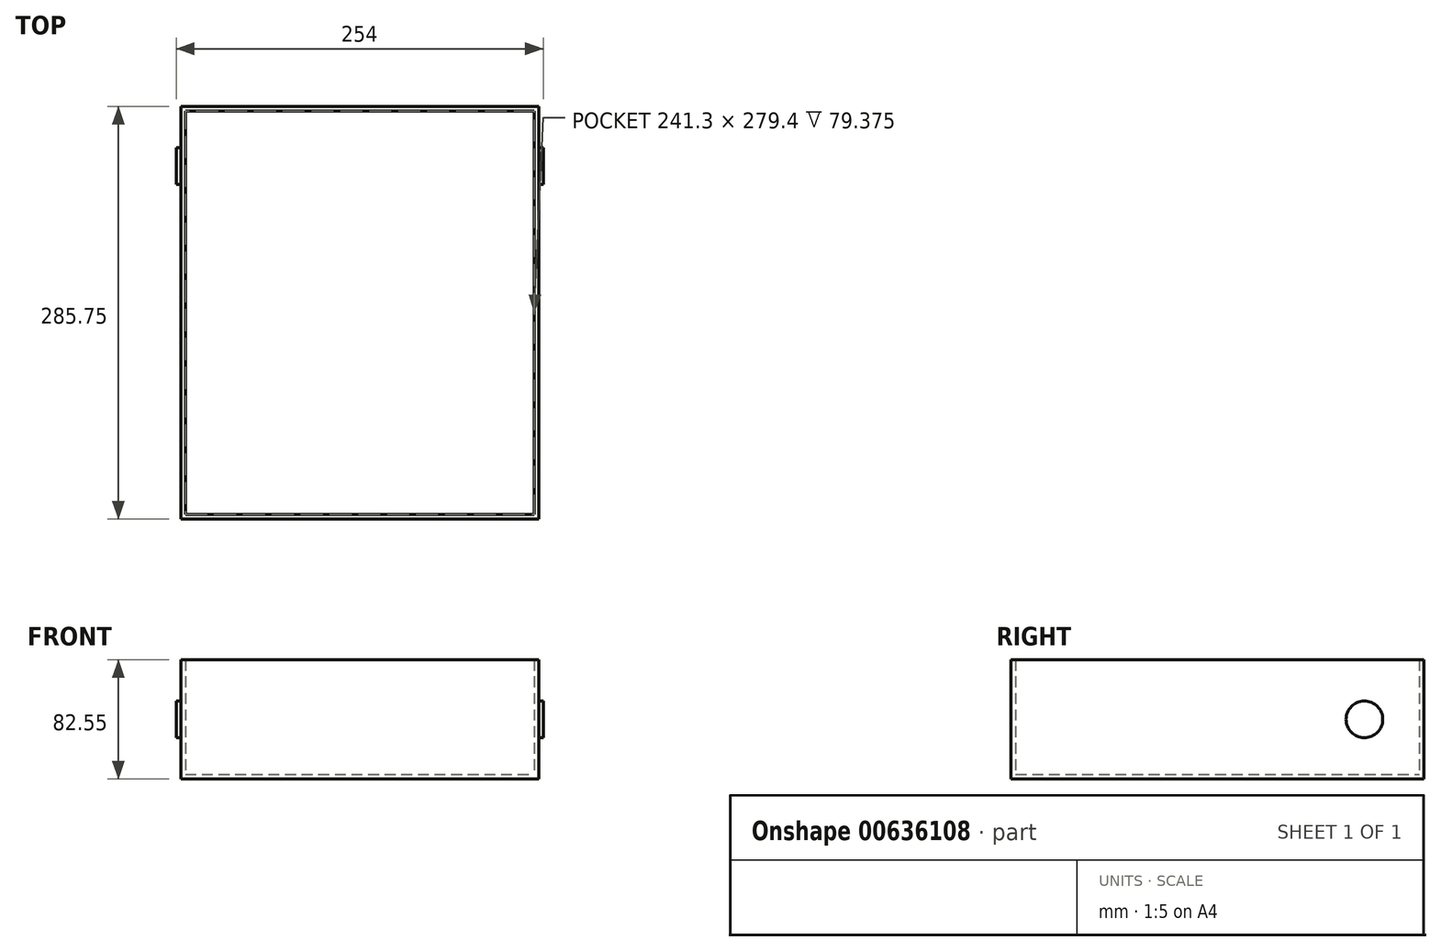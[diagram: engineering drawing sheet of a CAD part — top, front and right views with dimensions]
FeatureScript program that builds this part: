
annotation { "Feature Type Name" : "Feature", "Feature Type Description" : "" }
export const myFeature = defineFeature(function(context is Context, id is Id, definition is map)
    precondition{}
    {
        {
            var Q0;
            Q0=qCreatedBy(makeId("Top.planeOp"),FACE);
            var sketch = newSketch(context, id + "F0", { "sketchPlane" : qUnion([Q0])});
            skLineSegment(sketch, "E0.right", {"start": v(-132.22, 90.63) * mm, "end": v(-132.22, -188.77) * mm});
            skLineSegment(sketch, "E1.top", {"start": v(-132.22, 93.8) * mm, "end": v(112.25, 93.8) * mm});
            skLineSegment(sketch, "E1.left", {"start": v(-132.22, 90.63) * mm, "end": v(-132.22, 93.8) * mm});
            skLineSegment(sketch, "E2.bottom", {"start": v(112.25, 93.8) * mm, "end": v(115.43, 93.8) * mm});
            skLineSegment(sketch, "E2.right", {"start": v(115.43, 93.8) * mm, "end": v(115.43, -188.77) * mm});
            skLineSegment(sketch, "E3.top", {"start": v(-132.22, -191.95) * mm, "end": v(115.43, -191.95) * mm});
            skLineSegment(sketch, "E3.left", {"start": v(-132.22, -188.77) * mm, "end": v(-132.22, -191.95) * mm});
            skLineSegment(sketch, "E3.right", {"start": v(115.43, -188.77) * mm, "end": v(115.43, -191.95) * mm});
            skPoint(sketch, "E4.right.end.orphan", {"position": v(112.25, -188.77) * mm});
            skPoint(sketch, "E4.left.end.orphan", {"position": v(-129.05, -188.77) * mm});
            skPoint(sketch, "E4.bottom.end.orphan", {"position": v(112.25, 90.63) * mm});
            skSolve(sketch);
        }
        {
            var Q0;
            Q0=makeQuery(id+"F0.imprint","IMPRINT",FACE,{"disambiguationData":[TD([[makeQuery(id+"F0.imprint","IMPRINT",EDGE,{"derivedFrom":sQuery(id+"F0.wireOp",EDGE,"E0.right")}),1.0]])]});
            extrude(context, id + "F1", {"entities" : qUnion([Q0]), "depth" : 82.55 * mm, "offsetDistance" : 25.4 * mm});
        }
        {
            var Q0;
            Q0=makeQuery(id+"F1.opExtrude","CAP_FACE",FACE,{"disambiguationData":[OSD([sQuery(id+"F0.wireOp",EDGE,"E0.right"),sQuery(id+"F0.wireOp",EDGE,"E1.top"),sQuery(id+"F0.wireOp",EDGE,"E1.left"),sQuery(id+"F0.wireOp",EDGE,"E2.bottom"),sQuery(id+"F0.wireOp",EDGE,"E2.right"),sQuery(id+"F0.wireOp",EDGE,"E3.top"),sQuery(id+"F0.wireOp",EDGE,"E3.left"),sQuery(id+"F0.wireOp",EDGE,"E3.right")])],"isStart":false});
            shell(context, id + "F2", {"entities" : qUnion([Q0]), "thickness" : 3.17 * mm});
        }
        {
            var Q0;
            Q0=makeQuery(id+"F1.opExtrude","SWEPT_FACE",FACE,{"disambiguationData":[OSD([sQuery(id+"F0.wireOp",EDGE,"E2.right"),sQuery(id+"F0.wireOp",EDGE,"E3.right")])]});
            var sketch = newSketch(context, id + "F3", { "sketchPlane" : qUnion([Q0])});
            skLineSegment(sketch, "E5", {"start": v(93.8, 41.28) * mm, "end": v(65.23, 41.28) * mm});
            skLineSegment(sketch, "E6", {"start": v(52.53, 53.98) * mm, "end": v(52.53, 82.55) * mm});
            skCircle(sketch, "E7", {"center": v(52.53, 41.28) * mm, "radius": 12.7 * mm});
            skSolve(sketch);
        }
        {
            var Q0;
            Q0=makeQuery(id+"F1.opExtrude","SWEPT_FACE",FACE,{"disambiguationData":[OSD([sQuery(id+"F0.wireOp",EDGE,"E0.right"),sQuery(id+"F0.wireOp",EDGE,"E1.left"),sQuery(id+"F0.wireOp",EDGE,"E3.left")])]});
            var sketch = newSketch(context, id + "F4", { "sketchPlane" : qUnion([Q0])});
            skLineSegment(sketch, "E8", {"start": v(-93.8, 41.28) * mm, "end": v(-65.23, 41.28) * mm});
            skLineSegment(sketch, "E9", {"start": v(-52.53, 53.98) * mm, "end": v(-52.53, 82.55) * mm});
            skCircle(sketch, "E10", {"center": v(-52.53, 41.28) * mm, "radius": 12.7 * mm});
            skSolve(sketch);
        }
        {
            var Q0;
            {var subQ0=sQuery(id+"F3.wireOp",EDGE,"E7");var subQ1=makeQuery(id+"F3.imprint","INTERSECT",VERTEX,{"derivedFrom":[sQuery(id+"F3.wireOp",EDGE,"E5"),subQ0]});Q0=makeQuery(id+"F3.imprint","IMPRINT",FACE,{"disambiguationData":[TD([[makeQuery(id+"F3.imprint","IMPRINT",EDGE,{"disambiguationData":[TD([[subQ1,-1.0]])],"derivedFrom":subQ0}),1.0]])]});}
            extrude(context, id + "F5", {"entities" : qUnion([Q0]), "operationType" : NewBodyOperationType.ADD, "depth" : 3.17 * mm, "offsetDistance" : 25.4 * mm});
        }
        {
            var Q0;
            {var subQ0=sQuery(id+"F4.wireOp",EDGE,"E10");var subQ1=makeQuery(id+"F4.imprint","INTERSECT",VERTEX,{"derivedFrom":[sQuery(id+"F4.wireOp",EDGE,"E8"),subQ0]});Q0=makeQuery(id+"F4.imprint","IMPRINT",FACE,{"disambiguationData":[TD([[makeQuery(id+"F4.imprint","IMPRINT",EDGE,{"disambiguationData":[TD([[subQ1,1.0]])],"derivedFrom":subQ0}),1.0]])]});}
            extrude(context, id + "F6", {"entities" : qUnion([Q0]), "operationType" : NewBodyOperationType.ADD, "depth" : 3.17 * mm, "offsetDistance" : 25.4 * mm});
        }
    });
